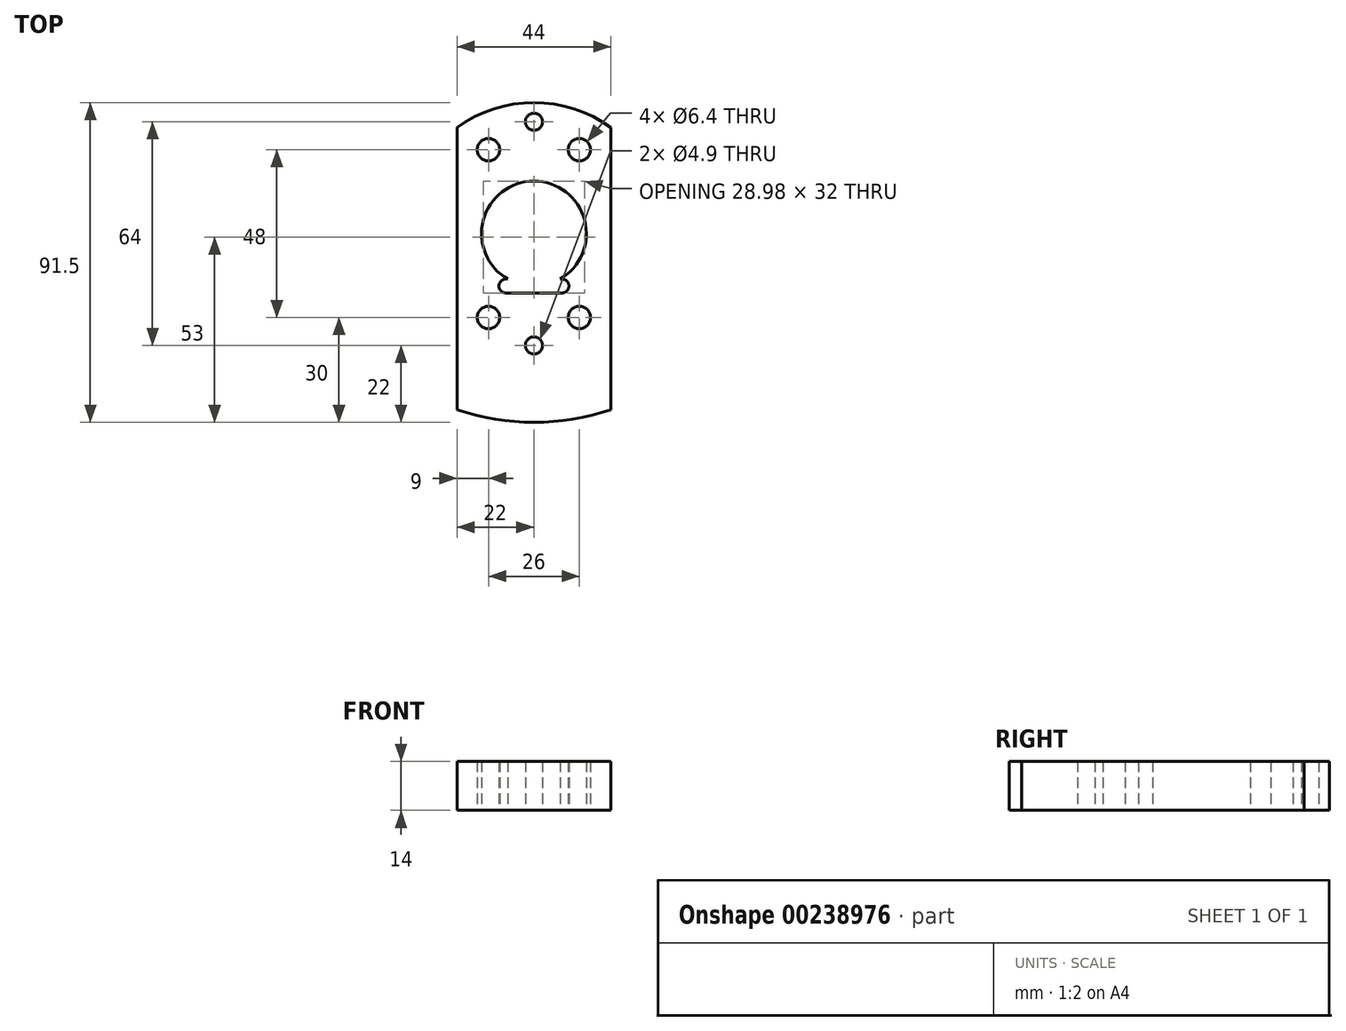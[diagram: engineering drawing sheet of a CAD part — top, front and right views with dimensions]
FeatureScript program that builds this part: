
annotation { "Feature Type Name" : "Feature", "Feature Type Description" : "" }
export const myFeature = defineFeature(function(context is Context, id is Id, definition is map)
    precondition{}
    {
        {
            var Q0;
            Q0=qCreatedBy(makeId("Top.planeOp"),FACE);
            var sketch = newSketch(context, id + "F0", { "sketchPlane" : qUnion([Q0])});
            skLineSegment(sketch, "E0", {"start": v(-22, 30.37) * mm, "end": v(-22, -50.4) * mm});
            skArc(sketch, "E1", {"start": v(-22.1, -50.37) * mm, "mid": v(0, -54) * mm, "end": v(22.1, -50.37) * mm});
            skLineSegment(sketch, "E2.MirrorCS", {"start": v(22, 30.37) * mm, "end": v(22, -50.4) * mm});
            skCircle(sketch, "E3", {"center": v(0, -32) * mm, "radius": 2.45 * mm});
            skCircle(sketch, "E4", {"center": v(0, 15) * mm, "radius": 55 * mm, "construction": true});
            skCircle(sketch, "E5", {"center": v(-13, -24) * mm, "radius": 3.2 * mm});
            skCircle(sketch, "E6.MirrorC", {"center": v(13, -24) * mm, "radius": 3.2 * mm});
            skCircle(sketch, "E7", {"center": v(0, 0) * mm, "radius": 23.5 * mm, "construction": true});
            skLineSegment(sketch, "E8", {"start": v(0, 15) * mm, "end": v(59.96, -19.62) * mm});
            skCircle(sketch, "E9", {"center": v(0, 15) * mm, "radius": 50 * mm, "construction": true});
            skCircle(sketch, "E10", {"center": v(43.3, -10) * mm, "radius": 20 * mm, "construction": true});
            skCircle(sketch, "E11", {"center": v(0, 65) * mm, "radius": 20 * mm, "construction": true});
            skCircle(sketch, "E12.MirrorC", {"center": v(-13, 24) * mm, "radius": 3.2 * mm});
            skCircle(sketch, "E13.MirrorC", {"center": v(13, 24) * mm, "radius": 3.2 * mm});
            skCircle(sketch, "E14.MirrorC", {"center": v(0, 32) * mm, "radius": 2.45 * mm});
            skArc(sketch, "E15.trimOffspring", {"start": v(22, 30.37) * mm, "mid": v(0, 37.5) * mm, "end": v(-22, 30.37) * mm});
            skCircle(sketch, "E16", {"center": v(0, 0) * mm, "radius": 15 * mm});
            skSolve(sketch);
        }
        {
            var Q0;
            Q0=qSketchRegion(id+"F0",true);
            extrude(context, id + "F1", {"entities" : qUnion([Q0]), "depth" : 7 * mm, "hasSecondDirection" : true, "secondDirectionOppositeDirection" : true, "secondDirectionDepth" : 7 * mm});
        }
        {
            var Q0;
            Q0=qCreatedBy(makeId("Top.planeOp"),FACE);
            var sketch = newSketch(context, id + "F2", { "sketchPlane" : qUnion([Q0])});
            skCircle(sketch, "E17", {"center": v(0, 0) * mm, "radius": 12.5 * mm, "construction": true});
            skLineSegment(sketch, "E18", {"start": v(-33.6, -12.5) * mm, "end": v(32.1, -12.5) * mm, "construction": true});
            skLineSegment(sketch, "E19", {"start": v(-8, -13) * mm, "end": v(0, -13) * mm});
            skLineSegment(sketch, "E20", {"start": v(0, -17) * mm, "end": v(-8, -17) * mm});
            skLineSegment(sketch, "E21", {"start": v(-8, -4.63) * mm, "end": v(-8, -31.33) * mm, "construction": true});
            skLineSegment(sketch, "E22", {"start": v(-25.25, -15) * mm, "end": v(7.52, -15) * mm, "construction": true});
            skArc(sketch, "E23", {"start": v(-8, -13) * mm, "mid": v(-10, -15) * mm, "end": v(-8, -17) * mm});
            skLineSegment(sketch, "E24.MirrorCS", {"start": v(8, -13) * mm, "end": v(0, -13) * mm});
            skLineSegment(sketch, "E25.MirrorCS", {"start": v(0, -17) * mm, "end": v(8, -17) * mm});
            skArc(sketch, "E26.MirrorCS", {"start": v(8, -13) * mm, "mid": v(10, -15) * mm, "end": v(8, -17) * mm});
            skSolve(sketch);
        }
        {
            var Q0;
            Q0=qSketchRegion(id+"F2",true);
            extrude(context, id + "F3", {"entities" : qUnion([Q0]), "operationType" : NewBodyOperationType.REMOVE, "depth" : 25 * mm, "hasSecondDirection" : true, "secondDirectionOppositeDirection" : true, "secondDirectionDepth" : 25 * mm});
        }
    });
